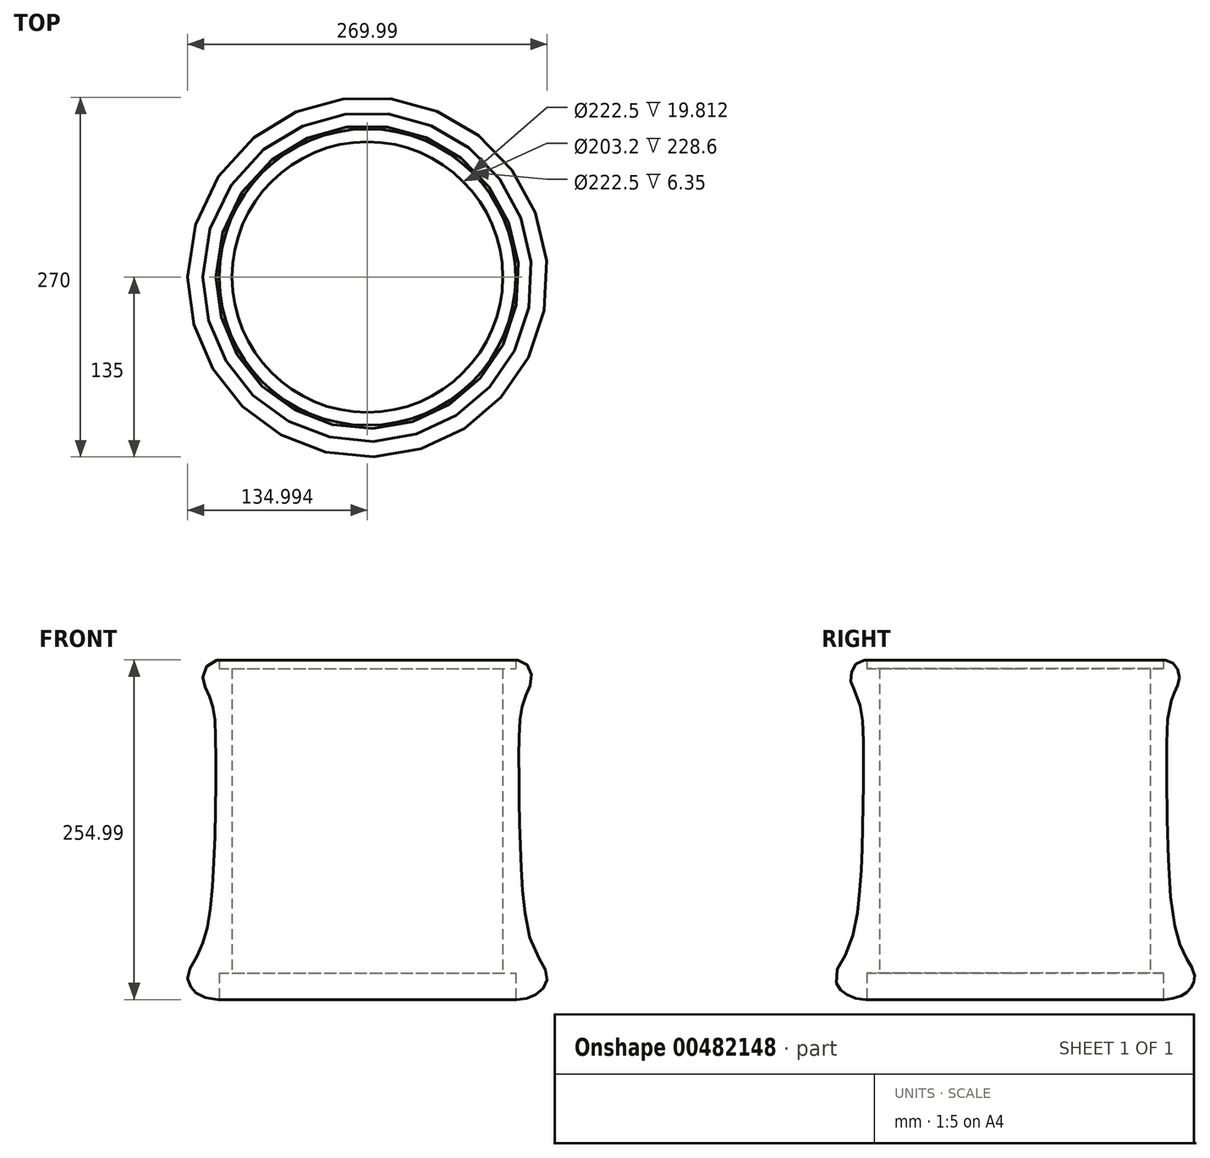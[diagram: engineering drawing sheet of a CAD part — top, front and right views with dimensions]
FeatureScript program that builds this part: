
annotation { "Feature Type Name" : "Feature", "Feature Type Description" : "" }
export const myFeature = defineFeature(function(context is Context, id is Id, definition is map)
    precondition{}
    {
        {
            var Q0;
            Q0=qCreatedBy(makeId("Front.planeOp"),FACE);
            var sketch = newSketch(context, id + "F0", { "sketchPlane" : qUnion([Q0])});
            skLineSegment(sketch, "E0", {"start": v(-1.2, -124.29) * mm, "end": v(8.44, -124.29) * mm});
            skLineSegment(sketch, "E1", {"start": v(8.44, -124.29) * mm, "end": v(8.44, 104.31) * mm});
            skLineSegment(sketch, "E2", {"start": v(8.44, 104.31) * mm, "end": v(-1.2, 104.31) * mm});
            skLineSegment(sketch, "E3", {"start": v(-1.2, 104.31) * mm, "end": v(-1.2, 110.66) * mm});
            skLineSegment(sketch, "E4", {"start": v(-1.2, -124.29) * mm, "end": v(-1.2, -144.1) * mm});
            skFitSpline(sketch, "E5", {"points": [v(-1.2, 110.66) * mm, v(-13, 100.92) * mm, v(-11.38, 89.94) * mm, v(-6.54, 78) * mm, v(-3.96, 55.4) * mm, v(-4.25, -12.38) * mm, v(-8.12, -78.55) * mm, v(-16.71, -109.48) * mm, v(-24.87, -125.8) * mm, v(-22.3, -134.83) * mm, v(-17.14, -139.99) * mm, v(-1.2, -144.1) * mm], "startDerivative": vector(-250.27, 57.52) * mm, "endDerivative": vector(246.37, 6.49) * mm});
            skLineSegment(sketch, "E6", {"start": v(8.44, -124.29) * mm, "end": v(110.04, -124.29) * mm, "construction": true});
            skLineSegment(sketch, "E7", {"start": v(110.04, -124.29) * mm, "end": v(110.04, 180.51) * mm, "construction": true});
            skLineSegment(sketch, "E8", {"start": v(110.04, -124.29) * mm, "end": v(110.04, -158.02) * mm, "construction": true});
            skSolve(sketch);
        }
        {
            var Q0;
            Q0=makeQuery(id+"F0.imprint","IMPRINT",FACE,{"disambiguationData":[TD([[makeQuery(id+"F0.imprint","IMPRINT",EDGE,{"derivedFrom":sQuery(id+"F0.wireOp",EDGE,"E0")}),1.0]])]});
            var Q1;
            Q1=sQuery(id+"F0.wireOp",EDGE,"E7");
            revolve(context, id + "F1", {"entities" : qUnion([Q0]), "axis" : qUnion([Q1]), "revolveType" : RevolveType.FULL});
        }
    });
